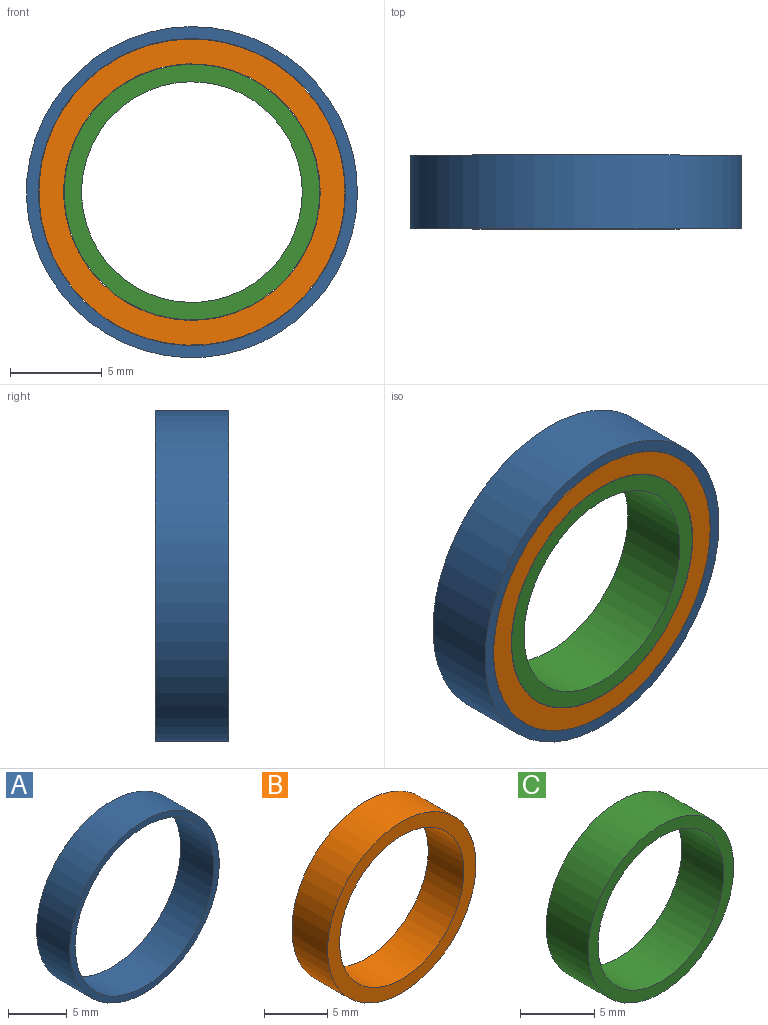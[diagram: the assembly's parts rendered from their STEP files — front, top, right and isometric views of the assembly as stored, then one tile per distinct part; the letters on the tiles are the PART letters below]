
ASSEMBLY  parts=3 mates=2
PART A: 4 faces, bbox 18x4x18 mm
  f0: cylinder r=8.35mm len=16.7mm, axis (0,1,0), area 209.9mm2, adj f2,f3
  f1: cylinder r=9mm len=18mm, axis (0,1,0), area 226.2mm2, adj f2,f3
  f2: plane 18x18mm, normal (0,-1,0), area 35.4mm2, adj f0,f1
  f3: plane 18x18mm, normal (0,1,0), area 35.4mm2, adj f0,f1
PART B: 4 faces, bbox 16.6x4x16.6 mm
  f0: cylinder r=6.98mm len=13.95mm, axis (0,1,0), area 175.3mm2, adj f2,f3
  f1: cylinder r=8.32mm len=16.65mm, axis (0,1,0), area 209.2mm2, adj f2,f3
  f2: plane 16.65x16.65mm, normal (0,-1,0), area 64.9mm2, adj f0,f1
  f3: plane 16.65x16.65mm, normal (0,1,0), area 64.9mm2, adj f0,f1
PART C: 4 faces, bbox 13.9x4x13.9 mm
  f0: cylinder r=6mm len=12mm, axis (0,1,0), area 150.8mm2, adj f2,f3
  f1: cylinder r=6.95mm len=13.9mm, axis (0,1,0), area 174.7mm2, adj f2,f3
  f2: plane 13.9x13.9mm, normal (0,-1,0), area 38.6mm2, adj f0,f1
  f3: plane 13.9x13.9mm, normal (0,1,0), area 38.6mm2, adj f0,f1
PLACE A rot(axis=(0,-1,0),97.7deg) t=(0,0,0)mm
PLACE B at identity
PLACE C at identity fixed
MATE revolute A.f0 <-> C.f0  axis (0,-1,0) through (0,-2,0)mm
MATE fastened B.f0 <-> C.f0  axis (0,1,0) through (0,-2,0)mm
